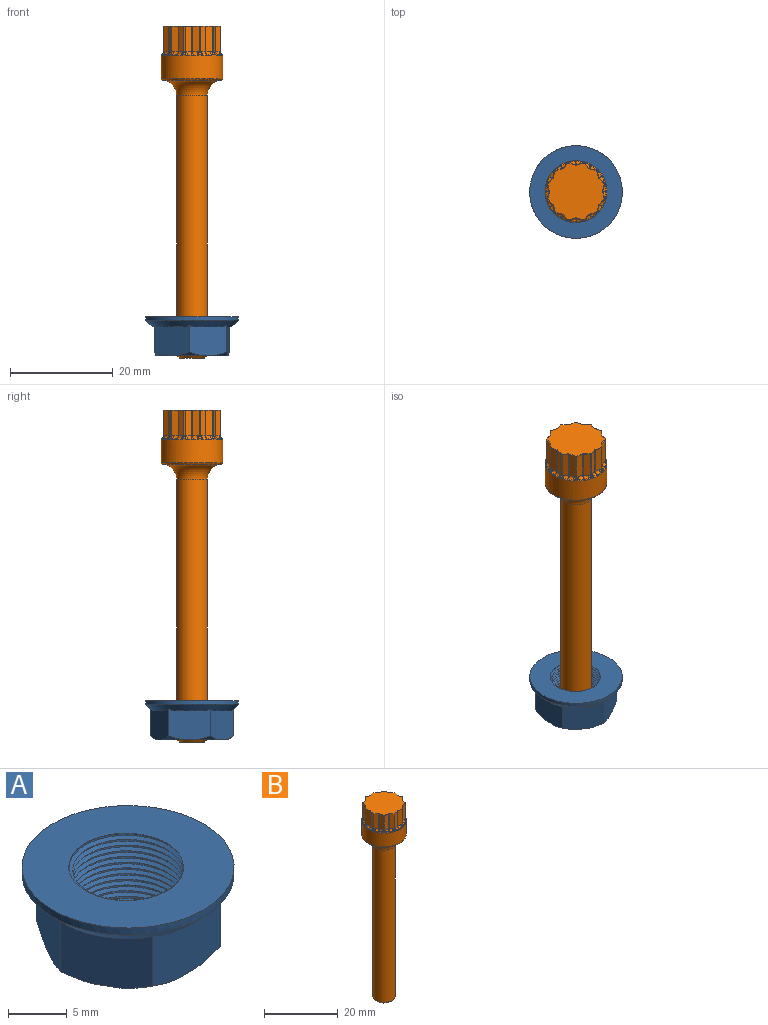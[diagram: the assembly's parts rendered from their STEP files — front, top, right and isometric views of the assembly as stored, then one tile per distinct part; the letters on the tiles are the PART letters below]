
ASSEMBLY  parts=2 mates=1
PART A: 29 faces, bbox 18.3x18.3x8.2 mm
  f0: plane 14.22x14mm, normal (0,0,-1), area 79.2mm2, adj f1,f2,f3,f4,f5,f6,f17,f18
  f1: plane 7.34x6.28mm, normal (-0.87,0.5,0), area 43.7mm2, adj f0,f2,f6,f7,f16,f18,f22
  f2: plane 7.34x6.28mm, normal (-0.87,-0.5,0), area 43.7mm2, adj f0,f1,f3,f15,f16,f21,f22
  f3: plane 8.43x6.28mm, normal (0,-1,0), area 43.7mm2, adj f0,f2,f4,f11,f16,f20,f21
  f4: plane 7.34x6.28mm, normal (0.87,-0.5,0), area 43.7mm2, adj f0,f3,f5,f10,f16,f19,f20
  f5: plane 7.34x6.28mm, normal (0.87,0.5,0), area 43.7mm2, adj f0,f4,f6,f9,f16,f17,f19
  f6: plane 8.43x6.28mm, normal (0,1,0), area 43.7mm2, adj f0,f1,f5,f8,f16,f17,f18
  f7: plane 5.76x3.33mm, normal (0,0,-1), area 3.4mm2, adj f1,f16
  f8: plane 6.65x0.75mm, normal (0,0,-1), area 3.4mm2, adj f6,f16
  f9: plane 5.76x3.33mm, normal (0,0,-1), area 3.4mm2, adj f5,f16
  f10: plane 5.76x3.33mm, normal (0,0,-1), area 3.4mm2, adj f4,f16
  f11: plane 6.65x0.75mm, normal (0,0,-1), area 3.4mm2, adj f3,f16
  f12: cylinder r=9mm len=18mm, axis (0,0,1), area 42.4mm2, adj f13,f16
  f13: plane 18.2x18.2mm, normal (0,0,1), area 178.6mm2, adj f12,f25,f27,f28
  f14: cylinder r=4.5mm len=9mm, axis (0,0,-1), area 7.1mm2, adj f23,f24,f26
  f15: plane 5.76x3.33mm, normal (0,0,-1), area 3.4mm2, adj f2,f16
  f16: cone r=9mm half-angle=45deg, axis (0,0,1), area 91.2mm2, adj f1,f2,f3,f4,f5,f6,f7,f8
  f17: cone r=8.83mm half-angle=52deg, axis (0,0,1), area 3.2mm2, adj f0,f5,f6
  f18: cone r=8.83mm half-angle=52deg, axis (0,0,1), area 3.2mm2, adj f0,f1,f6
  f19: cone r=8.83mm half-angle=52deg, axis (0,0,1), area 3.2mm2, adj f0,f4,f5
  f20: cone r=8.83mm half-angle=52deg, axis (0,0,1), area 3.2mm2, adj f0,f3,f4
  f21: cone r=8.83mm half-angle=52deg, axis (0,0,1), area 3.2mm2, adj f0,f2,f3
  f22: cone r=8.83mm half-angle=52deg, axis (0,0,1), area 3.2mm2, adj f0,f1,f2
  f23: cone r=4.5mm half-angle=45deg, axis (0,0,-1), area 21.1mm2, adj f0,f14,f24,f26
  f24: plane 0.68x0.53mm, normal (0,1,0), area 0.2mm2, adj f14,f23,f25,f26,f27,f28
  f25: bspline ~11.57x10.02mm, area 126.1mm2, adj f13,f24,f27,f28
  f26: bspline ~10.82x9.37mm, area 6.1mm2, adj f14,f23,f24,f27
  f27: bspline ~11.57x10.02mm, area 133.8mm2, adj f13,f24,f25,f26,f28
  f28: bspline ~11.64x10.08mm, area 80.9mm2, adj f13,f24,f25,f27
PART B: 259 faces, bbox 13x13x64.5 mm
  f0: plane 0.34x0.2mm, normal (0,0,1), area 0mm2, adj f126,f130,f163
  f1: plane 0.39x0.06mm, normal (0,0,1), area 0mm2, adj f125,f129,f175
  f2: plane 0.34x0.2mm, normal (0,0,1), area 0mm2, adj f114,f118,f151
  f3: plane 0.34x0.2mm, normal (0,0,1), area 0mm2, adj f113,f117,f187
  f4: plane 0.39x0.06mm, normal (0,0,1), area 0mm2, adj f102,f106,f139
  f5: plane 0.34x0.2mm, normal (0,0,1), area 0mm2, adj f101,f105,f199
  f6: plane 0.34x0.2mm, normal (0,0,1), area 0mm2, adj f90,f94,f140
  f7: plane 0.39x0.06mm, normal (0,0,1), area 0mm2, adj f89,f93,f200
  f8: plane 0.34x0.2mm, normal (0,0,1), area 0mm2, adj f78,f82,f152
  f9: plane 0.34x0.2mm, normal (0,0,1), area 0mm2, adj f77,f81,f188
  f10: plane 0.39x0.06mm, normal (0,0,1), area 0mm2, adj f66,f70,f164
  f11: plane 4.96x0.95mm, normal (0.71,0.71,0), area 6.6mm2, adj f47,f48,f63,f65,f252
  f12: plane 4.96x1.29mm, normal (-0.26,0.97,0), area 6.6mm2, adj f36,f48,f64,f66,f253
  f13: plane 4.96x1.29mm, normal (0.26,0.97,0), area 6.6mm2, adj f36,f49,f70,f72,f249
  f14: plane 4.96x0.95mm, normal (-0.71,0.71,0), area 6.6mm2, adj f37,f49,f76,f78,f245
  f15: plane 4.96x1.29mm, normal (-0.26,0.97,0), area 6.6mm2, adj f37,f50,f82,f84,f241
  f16: plane 4.96x1.29mm, normal (-0.97,0.26,0), area 6.6mm2, adj f38,f50,f88,f90,f237
  f17: plane 4.96x0.95mm, normal (-0.71,0.71,0), area 6.6mm2, adj f38,f51,f94,f96,f233
  f18: plane 4.96x1.29mm, normal (-0.97,-0.26,0), area 6.6mm2, adj f39,f51,f100,f102,f229
  f19: plane 4.96x1.29mm, normal (-0.97,0.26,0), area 6.6mm2, adj f39,f52,f106,f108,f225
  f20: plane 4.96x0.95mm, normal (-0.71,-0.71,0), area 6.6mm2, adj f40,f52,f112,f114,f221
  f21: plane 4.96x1.29mm, normal (-0.97,-0.26,0), area 6.6mm2, adj f40,f53,f118,f120,f217
  f22: plane 4.96x1.29mm, normal (-0.26,-0.97,0), area 6.6mm2, adj f41,f53,f124,f126,f213
  f23: plane 4.96x0.95mm, normal (-0.71,-0.71,0), area 6.6mm2, adj f41,f54,f130,f132,f209
  f24: plane 4.96x1.29mm, normal (0.26,-0.97,0), area 6.6mm2, adj f42,f54,f129,f131,f208
  f25: plane 4.96x1.29mm, normal (-0.26,-0.97,0), area 6.6mm2, adj f42,f55,f123,f125,f212
  f26: plane 4.96x0.95mm, normal (0.71,-0.71,0), area 6.6mm2, adj f43,f55,f117,f119,f216
  f27: plane 4.96x1.29mm, normal (0.26,-0.97,0), area 6.6mm2, adj f43,f56,f111,f113,f220
  f28: plane 4.96x1.29mm, normal (0.97,-0.26,0), area 6.6mm2, adj f44,f56,f105,f107,f224
  f29: plane 4.96x0.95mm, normal (0.71,-0.71,0), area 6.6mm2, adj f44,f57,f99,f101,f228
  f30: plane 4.96x1.29mm, normal (0.97,0.26,0), area 6.6mm2, adj f45,f57,f93,f95,f232
  f31: plane 4.96x1.29mm, normal (0.97,-0.26,0), area 6.6mm2, adj f45,f58,f87,f89,f236
  f32: plane 4.96x0.95mm, normal (0.71,0.71,0), area 6.6mm2, adj f46,f58,f81,f83,f240
  f33: plane 4.96x1.29mm, normal (0.97,0.26,0), area 6.6mm2, adj f46,f59,f75,f77,f244
  f34: plane 4.96x1.29mm, normal (0.26,0.97,0), area 6.6mm2, adj f47,f59,f69,f71,f248
  f35: plane 10.97x10.97mm, normal (0,0,1), area 90.5mm2, adj f207,f208,f209,f210,f211,f212,f213,f214
  f36: cylinder r=0.25mm len=4.94mm, axis (0,0,-1), area 0.6mm2, adj f12,f13,f68,f251
  f37: cylinder r=0.25mm len=4.94mm, axis (0,0,1), area 0.6mm2, adj f14,f15,f80,f243
  f38: cylinder r=0.25mm len=4.94mm, axis (0,0,-1), area 0.6mm2, adj f16,f17,f92,f235
  f39: cylinder r=0.25mm len=4.94mm, axis (0,0,-1), area 0.6mm2, adj f18,f19,f104,f227
  f40: cylinder r=0.25mm len=4.94mm, axis (0,0,1), area 0.6mm2, adj f20,f21,f116,f219
  f41: cylinder r=0.25mm len=4.94mm, axis (0,0,-1), area 0.6mm2, adj f22,f23,f128,f211
  f42: cylinder r=0.25mm len=4.94mm, axis (0,0,1), area 0.6mm2, adj f24,f25,f127,f210
  f43: cylinder r=0.25mm len=4.94mm, axis (0,0,-1), area 0.6mm2, adj f26,f27,f115,f218
  f44: cylinder r=0.25mm len=4.94mm, axis (0,0,1), area 0.6mm2, adj f28,f29,f103,f226
  f45: cylinder r=0.25mm len=4.94mm, axis (0,0,1), area 0.6mm2, adj f30,f31,f91,f234
  f46: cylinder r=0.25mm len=4.94mm, axis (0,0,-1), area 0.6mm2, adj f32,f33,f79,f242
  f47: cylinder r=0.25mm len=4.94mm, axis (0,0,-1), area 0.6mm2, adj f11,f34,f67,f250
  f48: cylinder r=0.25mm len=4.96mm, axis (0,0,-1), area 1.3mm2, adj f11,f12,f62,f254
  f49: cylinder r=0.25mm len=4.96mm, axis (0,0,1), area 1.3mm2, adj f13,f14,f74,f247
  f50: cylinder r=0.25mm len=4.96mm, axis (0,0,1), area 1.3mm2, adj f15,f16,f86,f239
  f51: cylinder r=0.25mm len=4.96mm, axis (0,0,1), area 1.3mm2, adj f17,f18,f98,f231
  f52: cylinder r=0.25mm len=4.96mm, axis (0,0,1), area 1.3mm2, adj f19,f20,f110,f223
  f53: cylinder r=0.25mm len=4.96mm, axis (0,0,-1), area 1.3mm2, adj f21,f22,f122,f215
  f54: cylinder r=0.25mm len=4.96mm, axis (0,0,1), area 1.3mm2, adj f23,f24,f133,f207
  f55: cylinder r=0.25mm len=4.96mm, axis (0,0,-1), area 1.3mm2, adj f25,f26,f121,f214
  f56: cylinder r=0.25mm len=4.96mm, axis (0,0,1), area 1.3mm2, adj f27,f28,f109,f222
  f57: cylinder r=0.25mm len=4.96mm, axis (0,0,1), area 1.3mm2, adj f29,f30,f97,f230
  f58: cylinder r=0.25mm len=4.96mm, axis (0,0,1), area 1.3mm2, adj f31,f32,f85,f238
  f59: cylinder r=0.25mm len=4.96mm, axis (0,0,1), area 1.3mm2, adj f33,f34,f73,f246
  f60: cylinder r=6mm len=12mm, axis (0,0,1), area 171.3mm2, adj f134,f135,f136,f137,f138,f139,f140,f141
  f61: plane 0.34x0.2mm, normal (0,0,1), area 0mm2, adj f65,f69,f176
  f62: bspline ~1.03x0.54mm, area 0.3mm2, adj f48,f63,f64,f170
  f63: bspline ~1.27x0.93mm, area 0.3mm2, adj f11,f62,f65,f172
  f64: bspline ~0.75x0.56mm, area 0.2mm2, adj f12,f62,f66,f168
  f65: cylinder r=0.5mm len=1.05mm, axis (-0.71,0.71,0), area 0.7mm2, adj f11,f61,f63,f67,f174
  f66: cylinder r=0.5mm len=1.09mm, axis (-0.97,-0.26,0), area 0.7mm2, adj f10,f12,f64,f68,f166
  f67: bspline ~0.57x0.47mm, area 0mm2, adj f47,f65,f69
  f68: bspline ~0.57x0.52mm, area 0mm2, adj f36,f66,f70
  f69: cylinder r=0.5mm len=1.09mm, axis (-0.97,0.26,0), area 0.7mm2, adj f34,f61,f67,f71,f178
  f70: cylinder r=0.5mm len=1.09mm, axis (-0.97,0.26,0), area 0.7mm2, adj f10,f13,f68,f72,f162
  f71: bspline ~0.71x0.7mm, area 0.2mm2, adj f34,f69,f73,f180
  f72: bspline ~0.75x0.56mm, area 0.2mm2, adj f13,f70,f74,f160
  f73: bspline ~0.79x0.76mm, area 0.3mm2, adj f59,f71,f75,f182
  f74: bspline ~1.03x0.54mm, area 0.3mm2, adj f49,f72,f76,f158
  f75: bspline ~0.71x0.7mm, area 0.2mm2, adj f33,f73,f77,f184
  f76: bspline ~1.27x0.93mm, area 0.3mm2, adj f14,f74,f78,f156
  f77: cylinder r=0.5mm len=1.09mm, axis (-0.26,0.97,0), area 0.7mm2, adj f9,f33,f75,f79,f186
  f78: cylinder r=0.5mm len=1.05mm, axis (-0.71,-0.71,0), area 0.7mm2, adj f8,f14,f76,f80,f154
  f79: bspline ~0.57x0.47mm, area 0mm2, adj f46,f77,f81
  f80: bspline ~0.57x0.47mm, area 0mm2, adj f37,f78,f82
  f81: cylinder r=0.5mm len=1.05mm, axis (-0.71,0.71,0), area 0.7mm2, adj f9,f32,f79,f83,f190
  f82: cylinder r=0.5mm len=1.09mm, axis (-0.97,-0.26,0), area 0.7mm2, adj f8,f15,f80,f84,f150
  f83: bspline ~1.27x0.93mm, area 0.3mm2, adj f32,f81,f85,f192
  f84: bspline ~0.71x0.7mm, area 0.2mm2, adj f15,f82,f86,f148
  f85: bspline ~1.02x0.54mm, area 0.3mm2, adj f58,f83,f87,f194
  f86: bspline ~0.79x0.76mm, area 0.3mm2, adj f50,f84,f88,f146
  f87: bspline ~0.75x0.56mm, area 0.2mm2, adj f31,f85,f89,f196
  f88: bspline ~0.71x0.7mm, area 0.2mm2, adj f16,f86,f90,f144
  f89: cylinder r=0.5mm len=1.09mm, axis (0.26,0.97,0), area 0.7mm2, adj f7,f31,f87,f91,f198
  f90: cylinder r=0.5mm len=1.09mm, axis (-0.26,-0.97,0), area 0.7mm2, adj f6,f16,f88,f92,f142
  f91: bspline ~0.57x0.52mm, area 0mm2, adj f45,f89,f93
  f92: bspline ~0.57x0.47mm, area 0mm2, adj f38,f90,f94
  f93: cylinder r=0.5mm len=1.09mm, axis (-0.26,0.97,0), area 0.7mm2, adj f7,f30,f91,f95,f202
  f94: cylinder r=0.5mm len=1.05mm, axis (-0.71,-0.71,0), area 0.7mm2, adj f6,f17,f92,f96,f138
  f95: bspline ~0.75x0.56mm, area 0.2mm2, adj f30,f93,f97,f204
  f96: bspline ~1.27x0.93mm, area 0.3mm2, adj f17,f94,f98,f136
  f97: bspline ~1.02x0.54mm, area 0.3mm2, adj f57,f95,f99,f205
  f98: bspline ~1.03x0.54mm, area 0.3mm2, adj f51,f96,f100,f134
  f99: bspline ~1.27x0.93mm, area 0.3mm2, adj f29,f97,f101,f203
  f100: bspline ~0.75x0.56mm, area 0.2mm2, adj f18,f98,f102,f135
  f101: cylinder r=0.5mm len=1.05mm, axis (0.71,0.71,0), area 0.7mm2, adj f5,f29,f99,f103,f201
  f102: cylinder r=0.5mm len=1.09mm, axis (0.26,-0.97,0), area 0.7mm2, adj f4,f18,f100,f104,f137
  f103: bspline ~0.57x0.47mm, area 0mm2, adj f44,f101,f105
  f104: bspline ~0.57x0.52mm, area 0mm2, adj f39,f102,f106
  f105: cylinder r=0.5mm len=1.09mm, axis (0.26,0.97,0), area 0.7mm2, adj f5,f28,f103,f107,f197
  f106: cylinder r=0.5mm len=1.09mm, axis (-0.26,-0.97,0), area 0.7mm2, adj f4,f19,f104,f108,f141
  f107: bspline ~0.71x0.7mm, area 0.2mm2, adj f28,f105,f109,f195
  f108: bspline ~0.75x0.56mm, area 0.2mm2, adj f19,f106,f110,f143
  f109: bspline ~0.79x0.76mm, area 0.3mm2, adj f56,f107,f111,f193
  f110: bspline ~1.02x0.54mm, area 0.3mm2, adj f52,f108,f112,f145
  f111: bspline ~0.71x0.7mm, area 0.2mm2, adj f27,f109,f113,f191
  f112: bspline ~1.27x0.93mm, area 0.3mm2, adj f20,f110,f114,f147
  f113: cylinder r=0.5mm len=1.09mm, axis (0.97,0.26,0), area 0.7mm2, adj f3,f27,f111,f115,f189
  f114: cylinder r=0.5mm len=1.05mm, axis (0.71,-0.71,0), area 0.7mm2, adj f2,f20,f112,f116,f149
  f115: bspline ~0.57x0.47mm, area 0mm2, adj f43,f113,f117
  f116: bspline ~0.57x0.47mm, area 0mm2, adj f40,f114,f118
  f117: cylinder r=0.5mm len=1.05mm, axis (0.71,0.71,0), area 0.7mm2, adj f3,f26,f115,f119,f185
  f118: cylinder r=0.5mm len=1.09mm, axis (0.26,-0.97,0), area 0.7mm2, adj f2,f21,f116,f120,f153
  f119: bspline ~1.27x0.93mm, area 0.3mm2, adj f26,f117,f121,f183
  f120: bspline ~0.71x0.7mm, area 0.2mm2, adj f21,f118,f122,f155
  f121: bspline ~1.03x0.54mm, area 0.3mm2, adj f55,f119,f123,f181
  f122: bspline ~0.79x0.76mm, area 0.3mm2, adj f53,f120,f124,f157
  f123: bspline ~0.75x0.56mm, area 0.2mm2, adj f25,f121,f125,f179
  f124: bspline ~0.71x0.7mm, area 0.2mm2, adj f22,f122,f126,f159
  f125: cylinder r=0.5mm len=1.09mm, axis (0.97,-0.26,0), area 0.7mm2, adj f1,f25,f123,f127,f177
  f126: cylinder r=0.5mm len=1.09mm, axis (0.97,-0.26,0), area 0.7mm2, adj f0,f22,f124,f128,f161
  f127: bspline ~0.57x0.52mm, area 0mm2, adj f42,f125,f129
  f128: bspline ~0.57x0.47mm, area 0mm2, adj f41,f126,f130
  f129: cylinder r=0.5mm len=1.09mm, axis (0.97,0.26,0), area 0.7mm2, adj f1,f24,f127,f131,f173
  f130: cylinder r=0.5mm len=1.05mm, axis (0.71,-0.71,0), area 0.7mm2, adj f0,f23,f128,f132,f165
  f131: bspline ~0.75x0.56mm, area 0.2mm2, adj f24,f129,f133,f171
  f132: bspline ~1.27x0.93mm, area 0.3mm2, adj f23,f130,f133,f167
  f133: bspline ~1.03x0.54mm, area 0.3mm2, adj f54,f131,f132,f169
  f134: bspline ~0.61x0.29mm, area 0mm2, adj f60,f98,f135,f136
  f135: bspline ~0.67x0.31mm, area 0.1mm2, adj f60,f100,f134,f137
  f136: bspline ~0.51x0.34mm, area 0.1mm2, adj f60,f96,f134,f138
  f137: bspline ~2.22x0.38mm, area 0.3mm2, adj f60,f102,f135,f139
  f138: bspline ~1.97x1.27mm, area 0.3mm2, adj f60,f94,f136,f140
  f139: torus R=5.75mm, axis (0,0,1), area 0.2mm2, adj f4,f60,f137,f141
  f140: torus R=5.75mm, axis (0,0,1), area 0.2mm2, adj f6,f60,f138,f142
  f141: bspline ~2.22x0.38mm, area 0.3mm2, adj f60,f106,f139,f143
  f142: bspline ~1.98x1.24mm, area 0.3mm2, adj f60,f90,f140,f144
  f143: bspline ~0.5x0.27mm, area 0.1mm2, adj f60,f108,f141,f145
  f144: bspline ~0.44x0.34mm, area 0.1mm2, adj f60,f88,f142,f146
  f145: bspline ~0.62x0.26mm, area 0.1mm2, adj f60,f110,f143,f147
  f146: bspline ~0.55x0.54mm, area 0.1mm2, adj f60,f86,f144,f148
  f147: bspline ~0.63x0.43mm, area 0.1mm2, adj f60,f112,f145,f149
  f148: bspline ~0.47x0.36mm, area 0.1mm2, adj f60,f84,f146,f150
  f149: bspline ~1.97x1.27mm, area 0.3mm2, adj f60,f114,f147,f151
  f150: bspline ~1.29x0.9mm, area 0.3mm2, adj f60,f82,f148,f152
  f151: torus R=5.75mm, axis (0,0,1), area 0.2mm2, adj f2,f60,f149,f153
  f152: torus R=5.75mm, axis (0,0,1), area 0.2mm2, adj f8,f60,f150,f154
  f153: bspline ~1.08x0.76mm, area 0.3mm2, adj f60,f118,f151,f155
  f154: bspline ~1.97x1.27mm, area 0.3mm2, adj f60,f78,f152,f156
  f155: bspline ~0.47x0.36mm, area 0.1mm2, adj f60,f120,f153,f157
  f156: bspline ~0.63x0.43mm, area 0.1mm2, adj f60,f76,f154,f158
  f157: bspline ~0.55x0.55mm, area 0.1mm2, adj f60,f122,f155,f159
  f158: bspline ~0.66x0.29mm, area 0.1mm2, adj f60,f74,f156,f160
  f159: bspline ~0.44x0.34mm, area 0.1mm2, adj f60,f124,f157,f161
  f160: bspline ~0.5x0.27mm, area 0.1mm2, adj f60,f72,f158,f162
  f161: bspline ~1.98x1.24mm, area 0.3mm2, adj f60,f126,f159,f163
  f162: bspline ~2.22x0.38mm, area 0.3mm2, adj f60,f70,f160,f164
  f163: torus R=5.75mm, axis (0,0,1), area 0.2mm2, adj f0,f60,f161,f165
  f164: torus R=5.75mm, axis (0,0,1), area 0.2mm2, adj f10,f60,f162,f166
  f165: bspline ~1.97x1.27mm, area 0.3mm2, adj f60,f130,f163,f167
  f166: bspline ~2.22x0.38mm, area 0.3mm2, adj f60,f66,f164,f168
  f167: bspline ~0.51x0.34mm, area 0.1mm2, adj f60,f132,f165,f169
  f168: bspline ~0.67x0.31mm, area 0.1mm2, adj f60,f64,f166,f170
  f169: bspline ~0.7x0.3mm, area 0.3mm2, adj f60,f133,f167,f171
  f170: bspline ~0.61x0.29mm, area 0mm2, adj f60,f62,f168,f172
  f171: bspline ~0.72x0.31mm, area 0.1mm2, adj f60,f131,f169,f173
  f172: bspline ~0.51x0.34mm, area 0.1mm2, adj f60,f63,f170,f174
  f173: bspline ~2.22x0.38mm, area 0.3mm2, adj f60,f129,f171,f175
  f174: bspline ~1.97x1.27mm, area 0.3mm2, adj f60,f65,f172,f176
  f175: torus R=5.75mm, axis (0,0,1), area 0.2mm2, adj f1,f60,f173,f177
  f176: torus R=5.75mm, axis (0,0,1), area 0.2mm2, adj f60,f61,f174,f178
  f177: bspline ~2.22x0.38mm, area 0.3mm2, adj f60,f125,f175,f179
  f178: bspline ~1.98x1.24mm, area 0.3mm2, adj f60,f69,f176,f180
  f179: bspline ~0.5x0.27mm, area 0.1mm2, adj f60,f123,f177,f181
  f180: bspline ~0.44x0.34mm, area 0.1mm2, adj f60,f71,f178,f182
  f181: bspline ~0.66x0.29mm, area 0.1mm2, adj f60,f121,f179,f183
  f182: bspline ~0.55x0.54mm, area 0.1mm2, adj f60,f73,f180,f184
  f183: bspline ~0.63x0.43mm, area 0.1mm2, adj f60,f119,f181,f185
  f184: bspline ~0.47x0.36mm, area 0.1mm2, adj f60,f75,f182,f186
  f185: bspline ~1.97x1.27mm, area 0.3mm2, adj f60,f117,f183,f187
  f186: bspline ~1.98x1.24mm, area 0.3mm2, adj f60,f77,f184,f188
  f187: torus R=5.75mm, axis (0,0,1), area 0.2mm2, adj f3,f60,f185,f189
  f188: torus R=5.75mm, axis (0,0,1), area 0.2mm2, adj f9,f60,f186,f190
  f189: bspline ~1.29x0.9mm, area 0.3mm2, adj f60,f113,f187,f191
  f190: bspline ~1.97x1.27mm, area 0.3mm2, adj f60,f81,f188,f192
  f191: bspline ~0.47x0.36mm, area 0.1mm2, adj f60,f111,f189,f193
  f192: bspline ~0.63x0.43mm, area 0.1mm2, adj f60,f83,f190,f194
  f193: bspline ~0.55x0.54mm, area 0.1mm2, adj f60,f109,f191,f195
  f194: bspline ~0.62x0.26mm, area 0.1mm2, adj f60,f85,f192,f196
  f195: bspline ~0.44x0.34mm, area 0.1mm2, adj f60,f107,f193,f197
  f196: bspline ~0.5x0.27mm, area 0.1mm2, adj f60,f87,f194,f198
  f197: bspline ~1.98x1.24mm, area 0.3mm2, adj f60,f105,f195,f199
  f198: bspline ~2.22x0.38mm, area 0.3mm2, adj f60,f89,f196,f200
  f199: torus R=5.75mm, axis (0,0,1), area 0.2mm2, adj f5,f60,f197,f201
  f200: torus R=5.75mm, axis (0,0,1), area 0.2mm2, adj f7,f60,f198,f202
  f201: bspline ~1.97x1.27mm, area 0.3mm2, adj f60,f101,f199,f203
  f202: bspline ~2.22x0.38mm, area 0.3mm2, adj f60,f93,f200,f204
  f203: bspline ~0.51x0.34mm, area 0.1mm2, adj f60,f99,f201,f205
  f204: bspline ~0.67x0.31mm, area 0.1mm2, adj f60,f95,f202,f205
  f205: bspline ~0.66x0.29mm, area 0.1mm2, adj f60,f97,f203,f204
  f206: torus R=5.75mm, axis (0,0,1), area 13.9mm2, adj f60,f256
  f207: torus R=0.19mm, axis (0,0,1), area 0mm2, adj f35,f54,f208,f209
  f208: cylinder r=0.06mm len=1.31mm, axis (-0.97,-0.26,0), area 0.1mm2, adj f24,f35,f207,f210
  f209: cylinder r=0.06mm len=0.99mm, axis (-0.71,0.71,0), area 0.1mm2, adj f23,f35,f207,f211
  f210: torus R=0.31mm, axis (0,0,1), area 0mm2, adj f35,f42,f208,f212
  f211: torus R=0.31mm, axis (0,0,1), area 0mm2, adj f35,f41,f209,f213
  f212: cylinder r=0.06mm len=1.31mm, axis (-0.97,0.26,0), area 0.1mm2, adj f25,f35,f210,f214
  f213: cylinder r=0.06mm len=1.31mm, axis (-0.97,0.26,0), area 0.1mm2, adj f22,f35,f211,f215
  f214: torus R=0.19mm, axis (0,0,1), area 0mm2, adj f35,f55,f212,f216
  f215: torus R=0.19mm, axis (0,0,1), area 0mm2, adj f35,f53,f213,f217
  f216: cylinder r=0.06mm len=0.99mm, axis (-0.71,-0.71,0), area 0.1mm2, adj f26,f35,f214,f218
  f217: cylinder r=0.06mm len=1.31mm, axis (-0.26,0.97,0), area 0.1mm2, adj f21,f35,f215,f219
  f218: torus R=0.31mm, axis (0,0,1), area 0mm2, adj f35,f43,f216,f220
  f219: torus R=0.31mm, axis (0,0,1), area 0mm2, adj f35,f40,f217,f221
  f220: cylinder r=0.06mm len=1.31mm, axis (-0.97,-0.26,0), area 0.1mm2, adj f27,f35,f218,f222
  f221: cylinder r=0.06mm len=0.99mm, axis (-0.71,0.71,0), area 0.1mm2, adj f20,f35,f219,f223
  f222: torus R=0.19mm, axis (0,0,1), area 0mm2, adj f35,f56,f220,f224
  f223: torus R=0.19mm, axis (0,0,1), area 0mm2, adj f35,f52,f221,f225
  f224: cylinder r=0.06mm len=1.31mm, axis (-0.26,-0.97,0), area 0.1mm2, adj f28,f35,f222,f226
  f225: cylinder r=0.06mm len=1.31mm, axis (0.26,0.97,0), area 0.1mm2, adj f19,f35,f223,f227
  f226: torus R=0.31mm, axis (0,0,1), area 0mm2, adj f35,f44,f224,f228
  f227: torus R=0.31mm, axis (0,0,1), area 0mm2, adj f35,f39,f225,f229
  f228: cylinder r=0.06mm len=0.99mm, axis (-0.71,-0.71,0), area 0.1mm2, adj f29,f35,f226,f230
  f229: cylinder r=0.06mm len=1.31mm, axis (-0.26,0.97,0), area 0.1mm2, adj f18,f35,f227,f231
  f230: torus R=0.19mm, axis (0,0,1), area 0mm2, adj f35,f57,f228,f232
  f231: torus R=0.19mm, axis (0,0,1), area 0mm2, adj f35,f51,f229,f233
  f232: cylinder r=0.06mm len=1.31mm, axis (0.26,-0.97,0), area 0.1mm2, adj f30,f35,f230,f234
  f233: cylinder r=0.06mm len=0.99mm, axis (0.71,0.71,0), area 0.1mm2, adj f17,f35,f231,f235
  f234: torus R=0.31mm, axis (0,0,1), area 0mm2, adj f35,f45,f232,f236
  f235: torus R=0.31mm, axis (0,0,1), area 0mm2, adj f35,f38,f233,f237
  f236: cylinder r=0.06mm len=1.31mm, axis (-0.26,-0.97,0), area 0.1mm2, adj f31,f35,f234,f238
  f237: cylinder r=0.06mm len=1.31mm, axis (0.26,0.97,0), area 0.1mm2, adj f16,f35,f235,f239
  f238: torus R=0.19mm, axis (0,0,1), area 0mm2, adj f35,f58,f236,f240
  f239: torus R=0.19mm, axis (0,0,1), area 0mm2, adj f35,f50,f237,f241
  f240: cylinder r=0.06mm len=0.99mm, axis (0.71,-0.71,0), area 0.1mm2, adj f32,f35,f238,f242
  f241: cylinder r=0.06mm len=1.31mm, axis (0.97,0.26,0), area 0.1mm2, adj f15,f35,f239,f243
  f242: torus R=0.31mm, axis (0,0,1), area 0mm2, adj f35,f46,f240,f244
  f243: torus R=0.31mm, axis (0,0,1), area 0mm2, adj f35,f37,f241,f245
  f244: cylinder r=0.06mm len=1.31mm, axis (0.26,-0.97,0), area 0.1mm2, adj f33,f35,f242,f246
  f245: cylinder r=0.06mm len=0.99mm, axis (0.71,0.71,0), area 0.1mm2, adj f14,f35,f243,f247
  f246: torus R=0.19mm, axis (0,0,1), area 0mm2, adj f35,f59,f244,f248
  f247: torus R=0.19mm, axis (0,0,1), area 0mm2, adj f35,f49,f245,f249
  f248: cylinder r=0.06mm len=1.31mm, axis (0.97,-0.26,0), area 0.1mm2, adj f34,f35,f246,f250
  f249: cylinder r=0.06mm len=1.31mm, axis (0.97,-0.26,0), area 0.1mm2, adj f13,f35,f247,f251
  f250: torus R=0.31mm, axis (0,0,1), area 0mm2, adj f35,f47,f248,f252
  f251: torus R=0.31mm, axis (0,0,1), area 0mm2, adj f35,f36,f249,f253
  f252: cylinder r=0.06mm len=0.99mm, axis (0.71,-0.71,0), area 0.1mm2, adj f11,f35,f250,f254
  f253: cylinder r=0.06mm len=1.31mm, axis (0.97,0.26,0), area 0.1mm2, adj f12,f35,f251,f254
  f254: torus R=0.19mm, axis (0,0,1), area 0mm2, adj f35,f48,f252,f253
  f255: cylinder r=3mm len=50.51mm, axis (0,0,1), area 952.1mm2, adj f256,f258
  f256: torus R=6mm, axis (0,0,-1), area 112.6mm2, adj f206,f255
  f257: plane 5x5mm, normal (0,0,-1), area 19.6mm2, adj f258
  f258: cone r=2.5mm half-angle=45deg, axis (0,0,1), area 12.2mm2, adj f255,f257
PLACE A rot(axis=(0,0,1),26.3deg) t=(-11.39,12.36,-15.59)mm
PLACE B rot(axis=(0,0,1),0.3deg) t=(-11.39,12.36,-14.65)mm
MATE cylindrical A.f12 <-> B.f255  axis (0,0,1) through (-11.39,12.36,-65.59)mm
